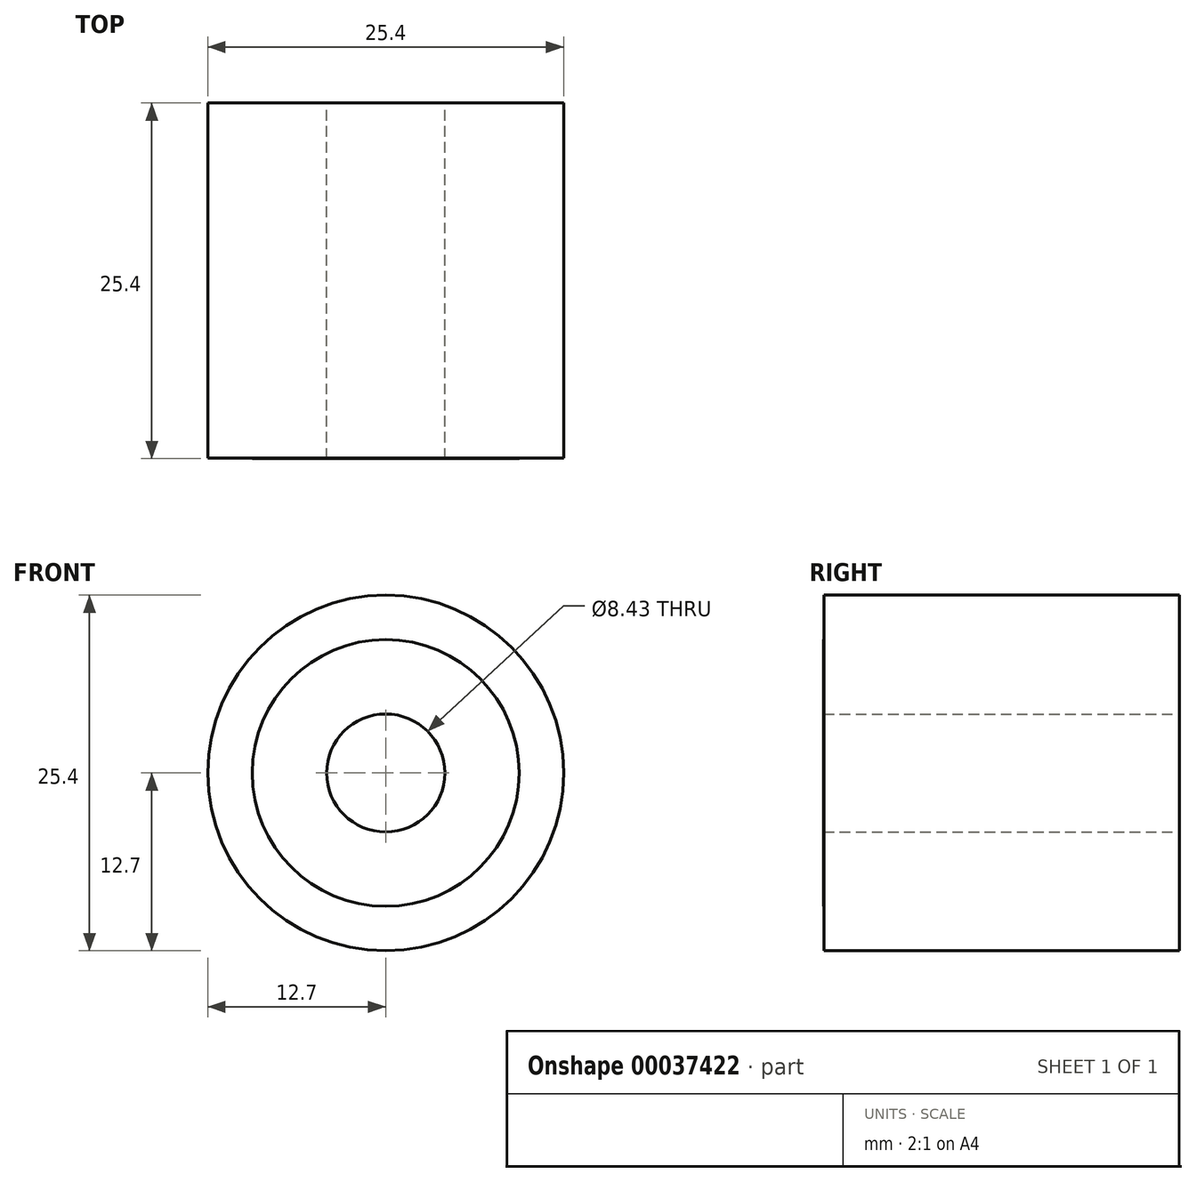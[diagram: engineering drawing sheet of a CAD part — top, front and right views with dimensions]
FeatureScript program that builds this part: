
annotation { "Feature Type Name" : "Feature", "Feature Type Description" : "" }
export const myFeature = defineFeature(function(context is Context, id is Id, definition is map)
    precondition{}
    {
        {
            var Q0;
            Q0=qCreatedBy(makeId("Front.planeOp"),FACE);
            var sketch = newSketch(context, id + "F0", { "sketchPlane" : qUnion([Q0])});
            skCircle(sketch, "E0", {"center": v(0, 0) * mm, "radius": 12.7 * mm});
            skCircle(sketch, "E1", {"center": v(0, 0) * mm, "radius": 4.22 * mm});
            skSolve(sketch);
        }
        {
            var Q0;
            Q0=makeQuery(id+"F0.imprint","IMPRINT",FACE,{"disambiguationData":[TD([[makeQuery(id+"F0.imprint","IMPRINT",EDGE,{"derivedFrom":sQuery(id+"F0.wireOp",EDGE,"E0")}),1.0]])]});
            extrude(context, id + "F1", {"entities" : qUnion([Q0]), "depth" : 25.4 * mm});
        }
        {
            var Q0;
            Q0=makeQuery(id+"F1.opExtrude","CAP_FACE",FACE,{"disambiguationData":[OSD([sQuery(id+"F0.wireOp",EDGE,"E0"),sQuery(id+"F0.wireOp",EDGE,"E1")])],"isStart":false});
            var sketch = newSketch(context, id + "F2", { "sketchPlane" : qUnion([Q0])});
            skCircle(sketch, "E2", {"center": v(0, 0) * mm, "radius": 9.53 * mm});
            skSolve(sketch);
        }
        {
            var Q0;
            Q0=makeQuery(id+"F2.imprint","IMPRINT",FACE,{"disambiguationData":[TD([[makeQuery(id+"F2.imprint","IMPRINT",EDGE,{"derivedFrom":sQuery(id+"F2.wireOp",EDGE,"E2")}),-1.0]])]});
            extrude(context, id + "F3", {"entities" : qUnion([Q0]), "operationType" : NewBodyOperationType.REMOVE, "oppositeDirection" : true, "depth" : 7 / 203.2 * mm});
        }
    });
